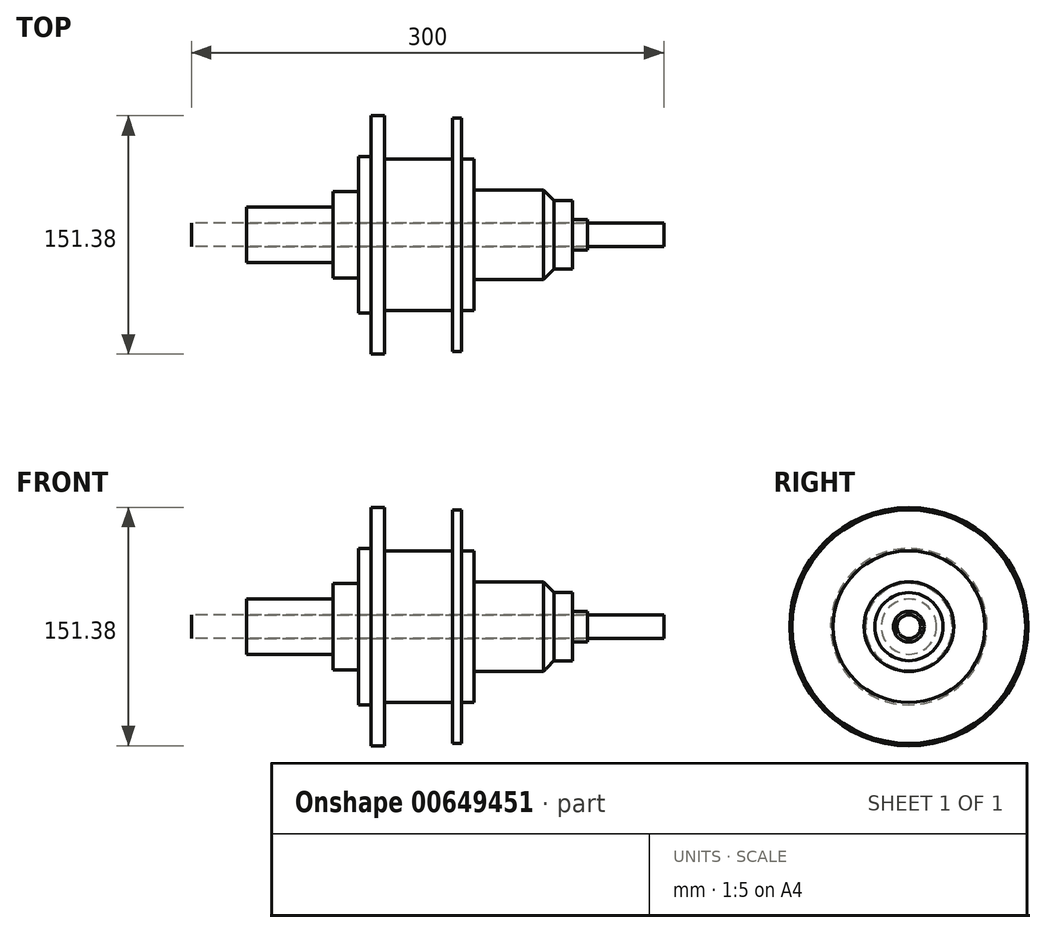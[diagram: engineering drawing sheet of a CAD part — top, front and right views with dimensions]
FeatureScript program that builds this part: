
annotation { "Feature Type Name" : "Feature", "Feature Type Description" : "" }
export const myFeature = defineFeature(function(context is Context, id is Id, definition is map)
    precondition{}
    {
        {
            var Q0;
            Q0=qCreatedBy(makeId("Right.planeOp"),FACE);
            var sketch = newSketch(context, id + "F0", { "sketchPlane" : qUnion([Q0])});
            skCircle(sketch, "E0", {"center": v(0, 0) * mm, "radius": 7.5 * mm});
            skSolve(sketch);
        }
        {
            var Q0;
            Q0=makeQuery(id+"F0.imprint","IMPRINT",FACE,{"disambiguationData":[TD([[makeQuery(id+"F0.imprint","IMPRINT",EDGE,{"derivedFrom":sQuery(id+"F0.wireOp",EDGE,"E0")}),1.0]])]});
            extrude(context, id + "F1", {"entities" : qUnion([Q0]), "depth" : 300 * mm, "offsetDistance" : 25 * mm, "symmetric" : true});
        }
        {
            var Q0;
            Q0=qCreatedBy(makeId("Front.planeOp"),FACE);
            var sketch = newSketch(context, id + "F2", { "sketchPlane" : qUnion([Q0])});
            skLineSegment(sketch, "E1", {"start": v(-115, 7.5) * mm, "end": v(-115, 17.5) * mm});
            skLineSegment(sketch, "E2", {"start": v(-115, 17.5) * mm, "end": v(-60, 17.5) * mm});
            skLineSegment(sketch, "E3", {"start": v(-60, 17.5) * mm, "end": v(-60, 27.5) * mm});
            skLineSegment(sketch, "E4", {"start": v(-60, 27.5) * mm, "end": v(-44, 27.5) * mm});
            skLineSegment(sketch, "E5", {"start": v(-44, 27.5) * mm, "end": v(-44, 49.69) * mm});
            skLineSegment(sketch, "E6", {"start": v(-44, 49.69) * mm, "end": v(-35.88, 49.69) * mm});
            skLineSegment(sketch, "E7", {"start": v(-35.88, 49.69) * mm, "end": v(-35.88, 75.69) * mm});
            skLineSegment(sketch, "E8", {"start": v(-35.88, 75.69) * mm, "end": v(-27.28, 75.69) * mm});
            skLineSegment(sketch, "E9", {"start": v(-27.28, 75.69) * mm, "end": v(-27.28, 48.19) * mm});
            skLineSegment(sketch, "E10", {"start": v(-27.28, 48.19) * mm, "end": v(0, 48.19) * mm});
            skLineSegment(sketch, "E11", {"start": v(0, 48.19) * mm, "end": v(15.84, 48.19) * mm});
            skLineSegment(sketch, "E12", {"start": v(15.84, 48.19) * mm, "end": v(15.84, 74.19) * mm});
            skLineSegment(sketch, "E13", {"start": v(15.84, 74.19) * mm, "end": v(21.47, 74.19) * mm});
            skLineSegment(sketch, "E14", {"start": v(21.47, 74.19) * mm, "end": v(21.47, 48.19) * mm});
            skLineSegment(sketch, "E15", {"start": v(21.47, 48.19) * mm, "end": v(29.6, 48.19) * mm});
            skLineSegment(sketch, "E16", {"start": v(29.6, 48.19) * mm, "end": v(29.6, 28.5) * mm});
            skLineSegment(sketch, "E17", {"start": v(29.6, 28.5) * mm, "end": v(73.66, 28.5) * mm});
            skLineSegment(sketch, "E18", {"start": v(73.66, 28.5) * mm, "end": v(80.22, 21.62) * mm});
            skLineSegment(sketch, "E19", {"start": v(80.22, 21.62) * mm, "end": v(92.1, 21.62) * mm});
            skLineSegment(sketch, "E20", {"start": v(92.1, 21.62) * mm, "end": v(92.1, 9.75) * mm});
            skLineSegment(sketch, "E21", {"start": v(92.1, 9.75) * mm, "end": v(101.72, 9.75) * mm});
            skLineSegment(sketch, "E22", {"start": v(101.72, 9.75) * mm, "end": v(101.72, 7.51) * mm});
            skLineSegment(sketch, "E23", {"start": v(101.72, 7.51) * mm, "end": v(-115, 7.5) * mm});
            skLineSegment(sketch, "E24", {"start": v(0, 0) * mm, "end": v(155.78, 0) * mm, "construction": true});
            skSolve(sketch);
        }
        {
            var Q0;
            Q0=makeQuery(id+"F2.imprint","IMPRINT",FACE,{"disambiguationData":[TD([[makeQuery(id+"F2.imprint","IMPRINT",EDGE,{"derivedFrom":sQuery(id+"F2.wireOp",EDGE,"E1")}),-1.0]])]});
            var Q1;
            Q1=makeQuery(id+"F1.opExtrude","SWEPT_FACE",FACE,{"disambiguationData":[OSD([sQuery(id+"F0.wireOp",EDGE,"E0")])]});
            revolve(context, id + "F3", {"entities" : qUnion([Q0]), "axis" : qUnion([Q1]), "revolveType" : RevolveType.FULL});
        }
    });
